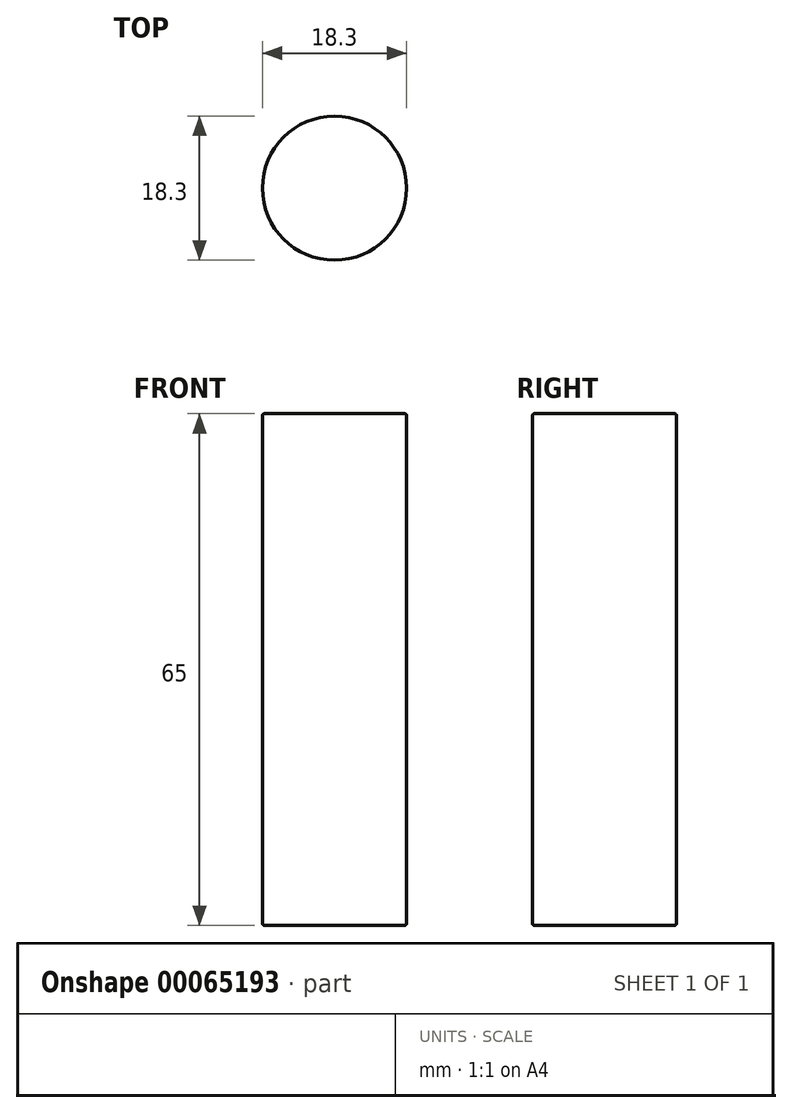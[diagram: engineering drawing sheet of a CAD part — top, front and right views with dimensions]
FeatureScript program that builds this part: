
annotation { "Feature Type Name" : "Feature", "Feature Type Description" : "" }
export const myFeature = defineFeature(function(context is Context, id is Id, definition is map)
    precondition{}
    {
        {
            var Q0;
            Q0=qCreatedBy(makeId("Top.planeOp"),FACE);
            var sketch = newSketch(context, id + "F0", { "sketchPlane" : qUnion([Q0])});
            skCircle(sketch, "E0", {"center": v(0, 0) * mm, "radius": 9.15 * mm});
            skSolve(sketch);
        }
        {
            var Q0;
            Q0=makeQuery(id+"F0.imprint","IMPRINT",FACE,{"disambiguationData":[TD([[makeQuery(id+"F0.imprint","IMPRINT",EDGE,{"derivedFrom":sQuery(id+"F0.wireOp",EDGE,"E0")}),1.0]])]});
            extrude(context, id + "F1", {"entities" : qUnion([Q0]), "depth" : 65 * mm});
        }
        {
            var Q0;
            Q0=makeQuery(id+"F1.opExtrude","CAP_EDGE",EDGE,{"disambiguationData":[OSD([sQuery(id+"F0.wireOp",EDGE,"E0")])],"isStart":false});
            var Q1;
            Q1=makeQuery(id+"F1.opExtrude","CAP_EDGE",EDGE,{"disambiguationData":[OSD([sQuery(id+"F0.wireOp",EDGE,"E0")])],"isStart":true});
            fillet(context, id + "F2", {"entities" : qUnion([Q0, Q1]), "radius" : .25 * mm, "tangentPropagation" : true, "allowEdgeOverflow" : false});
        }
    });
